# Revit family: oventrop_hydromat-dtr_1064804-16rfa
name_source: partatom
category: Арматура трубопроводов
revit_build: Autodesk Revit 2017 (Build: 20160225_1515(x64)
units: mm (PartAtom-declared; Revit-internal decimal feet)

## family parameters
Всегда вертикально = Да
Заголовок OmniClass = Adjusting/Controlling Valves for Liquid Services
На основе рабочей плоскости = Нет
Номер OmniClass = 23.65.55.14.17
Общий = Нет
При загрузке вырезать с полостями = Нет
Размер круглого соединителя = Использовать радиус
Тип детали = Клапан - Вставляется

## types (6) — shared parameters
Angle = 50.00°
Article Description = Differential pressure regulator
Article Type = Hydromat DTR 10648
BonnetPlastic = Color RGB 35-35-35
Bronze = Color RGB 156-122-90
Custom = Нет
D_Bonnet = 104 мм
EMCS Version = 2.0
ETIM Article Class = EC011463
Family Version = 10.14
Hb4 = 18 мм
Hb5 = 3 мм
Hlp1 = 22 мм
IFCExportAs = IfcValveType
IFCExportType = PRESSUREREDUCING
Lgt2 = 11 мм
MEPcontent Class = VALVE_BALANCING
Manufacturer URL = http://www.oventrop.de
Pressure Drop = 0.0 Па
Product Line = Oventrop
R1_Bonnet = 23.026 мм
R2_Bonnet = 31.2 мм
Rcut_Bonnet = 22.026 мм
Revit Version = 2015
r1 = 2 мм
r2 = 3 мм
r3_Bonnet = 14.857 мм
Группа модели = Hydromat DTR 10648
Изготовитель = Oventrop
Описание = Differential pressure regulator

## per-type parameters (varying)
- DN 40: Dist_elem=45 мм; Female_Port_Width=19.1 мм; GTIN=4026755333084; H1_Bonnet=43.076 мм; H_Bonnet=178 мм; Hb1=212.224 мм; Hb2=50 мм; Hb3=5 мм; Hb6=66.635 мм; Height=178 мм; L2=11.261 мм; Length=120 мм; Lgt1=21.1 мм; Manufacturer Art. No.=1064812; NominalDiameter=40.000 мм; Nut_Dimension=54 мм; Nut_Dimension2=58 мм; OuterDiameter=48.3 мм; Rad1=24.15 мм; Rad2=24.15 мм; Rad3=26.65 мм; Rad4=29.15 мм; Rad5=31.15 мм; SW1=66.973 мм; SW2=62.354 мм; URL=http://file-system.ru; t=18.1 мм
- DN 32: Dist_elem=45 мм; Female_Port_Width=19.1 мм; GTIN=4026755333077; H1_Bonnet=41.624 мм; H_Bonnet=172 мм; Hb1=204.392 мм; Hb2=50 мм; Hb3=1 мм; Hb6=63.734 мм; Height=172 мм; L2=9.886 мм; Length=110 мм; Lgt1=21.1 мм; Manufacturer Art. No.=1064810; NominalDiameter=32.000 мм; Nut_Dimension=50 мм; Nut_Dimension2=52 мм; OuterDiameter=42.4 мм; Rad1=21.2 мм; Rad2=21.2 мм; Rad3=23.7 мм; Rad4=26.2 мм; Rad5=28.2 мм; SW1=60.044 мм; SW2=57.735 мм; URL=www.stabiplan.com; t=16.34 мм
- DN 25: Dist_elem=39 мм; Female_Port_Width=16.8 мм; GTIN=4026755333060; H1_Bonnet=39.446 мм; H_Bonnet=163 мм; Hb1=192.643 мм; Hb2=25 мм; Hb3=13 мм; Hb6=48.793 мм; Height=163 мм; L2=7.857 мм; Length=110 мм; Lgt1=18.8 мм; Manufacturer Art. No.=1064808; NominalDiameter=25.000 мм; Nut_Dimension=41 мм; Nut_Dimension2=46 мм; OuterDiameter=33.7 мм; Rad1=16.85 мм; Rad2=16.85 мм; Rad3=19.35 мм; Rad4=21.85 мм; Rad5=23.85 мм; SW1=53.116 мм; SW2=47.343 мм; URL=www.stabiplan.com; t=14.8 мм
- DN 20: Dist_elem=40 мм; Female_Port_Width=14.5 мм; GTIN=4026755333053; H1_Bonnet=38.72 мм; H_Bonnet=160 мм; Hb1=188.727 мм; Hb2=22 мм; Hb3=11 мм; Hb6=43.716 мм; Height=160 мм; L2=6.272 мм; Length=93 мм; Lgt1=16.5 мм; Manufacturer Art. No.=1064806; NominalDiameter=20.000 мм; Nut_Dimension=32 мм; Nut_Dimension2=37 мм; OuterDiameter=26.9 мм; Rad1=13.45 мм; Rad2=13.45 мм; Rad3=15.95 мм; Rad4=18.45 мм; Rad5=20.45 мм; SW1=42.724 мм; SW2=36.95 мм; URL=www.stabiplan.com; t=13.7 мм
- DN 15: Dist_elem=37 мм; Female_Port_Width=13.2 мм; GTIN=4026755333046; H1_Bonnet=38.236 мм; H_Bonnet=158 мм; Hb1=186.116 мм; Hb2=19 мм; Hb3=15 мм; Hb6=46.472 мм; Height=158 мм; L2=4.966 мм; Length=88 мм; Lgt1=15.2 мм; Manufacturer Art. No.=1064804; NominalDiameter=15.000 мм; Nut_Dimension=27 мм; Nut_Dimension2=30 мм; OuterDiameter=21.3 мм; Rad1=10.65 мм; Rad2=10.65 мм; Rad3=13.15 мм; Rad4=15.65 мм; Rad5=17.65 мм; SW1=34.641 мм; SW2=31.177 мм; URL=www.stabiplan.com; t=12.6 мм
- DN 50: Dist_elem=67 мм; Female_Port_Width=25.7 мм; GTIN=4026755305593; H1_Bonnet=50.82 мм; H_Bonnet=210 мм; Hb1=253.997 мм; Hb2=50 мм; Hb3=5 мм; Hb6=63.735 мм; Height=210 мм; L2=14.059 мм; Length=150 мм; Lgt1=27.7 мм; Manufacturer Art. No.=1064816; NominalDiameter=50.000 мм; Nut_Dimension=65 мм; Nut_Dimension2=75 мм; OuterDiameter=60.3 мм; Rad1=30.15 мм; Rad2=30.15 мм; Rad3=32.65 мм; Rad4=35.15 мм; Rad5=37.15 мм; SW1=86.603 мм; SW2=75.056 мм; URL=www.stabiplan.com; t=20.3 мм

## geometry (parser evidence)
native form markers: Sweep x2
no freeform markers — native parametric forms only
